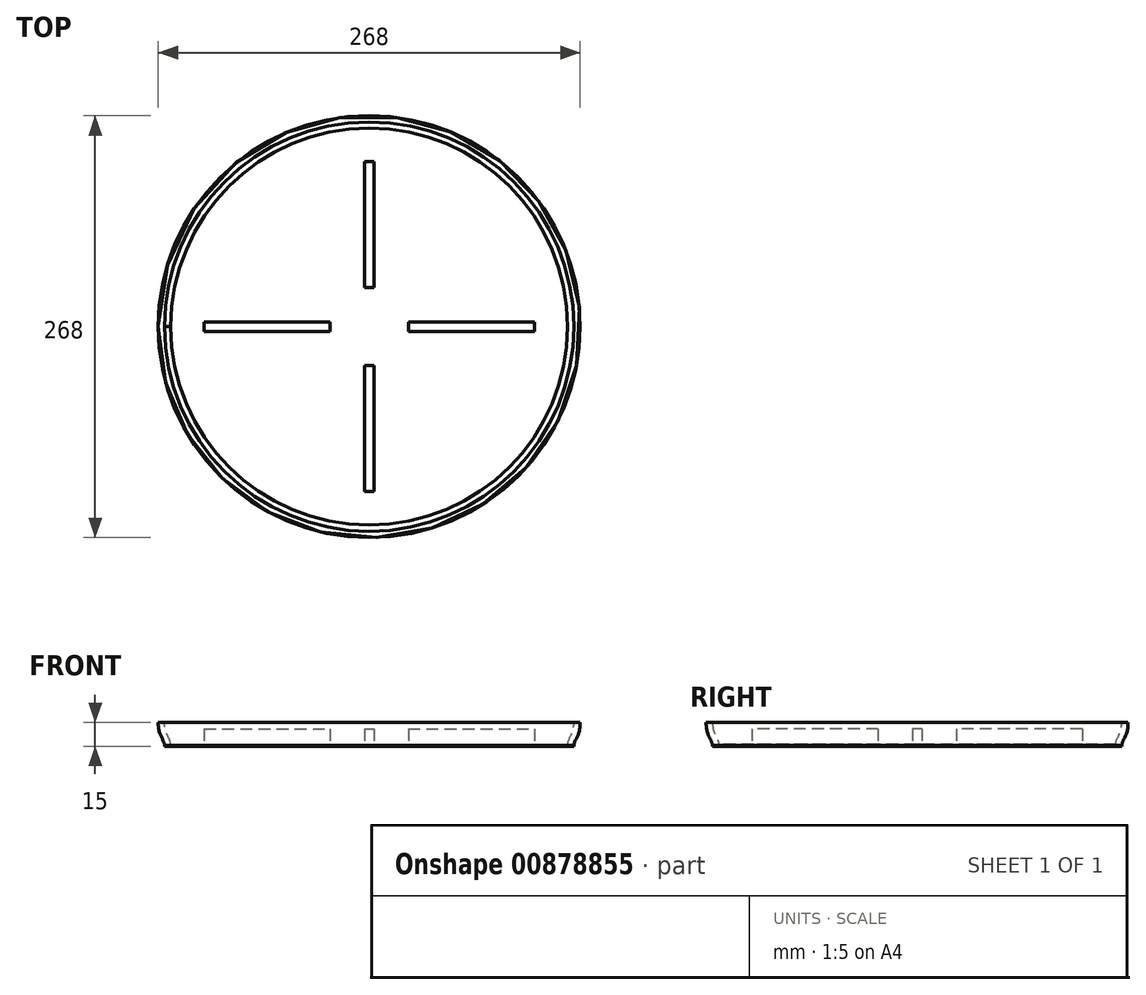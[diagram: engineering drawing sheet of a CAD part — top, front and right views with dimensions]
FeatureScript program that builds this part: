
annotation { "Feature Type Name" : "Feature", "Feature Type Description" : "" }
export const myFeature = defineFeature(function(context is Context, id is Id, definition is map)
    precondition{}
    {
        {
            var Q0;
            Q0=qCreatedBy(makeId("Top.planeOp"),FACE);
            var sketch = newSketch(context, id + "F0", { "sketchPlane" : qUnion([Q0])});
            skCircle(sketch, "E0", {"center": v(0, 0) * mm, "radius": 120 * mm, "construction": true});
            skCircle(sketch, "E1.0", {"center": v(0, 0) * mm, "radius": 126 * mm});
            skCircle(sketch, "E2.0", {"center": v(0, 0) * mm, "radius": 130 * mm});
            skSolve(sketch);
        }
        {
            var Q0;
            Q0=qCreatedBy(makeId("Front.planeOp"),FACE);
            var sketch = newSketch(context, id + "F1", { "sketchPlane" : qUnion([Q0])});
            skLineSegment(sketch, "E3", {"start": v(-126, 0) * mm, "end": v(-130, 0) * mm});
            skLineSegment(sketch, "E4", {"start": v(-126, 0) * mm, "end": v(-126, 13.8) * mm, "construction": true});
            skLineSegment(sketch, "E5", {"start": v(-130, 0) * mm, "end": v(-130, 15) * mm, "construction": true});
            skFitSpline(sketch, "E6", {"points": [v(-126, 0) * mm, v(-130, 15) * mm], "startDerivative": vector(0, 16.34) * mm, "endDerivative": vector(0, 22.5) * mm});
            skLineSegment(sketch, "E7", {"start": v(-130, 15) * mm, "end": v(-134, 15) * mm});
            skFitSpline(sketch, "E8.0", {"points": [v(-130, 0) * mm, v(-130, 0.44) * mm, v(-130.08, 1.18) * mm, v(-130.37, 2.24) * mm, v(-130.87, 3.47) * mm, v(-131.6, 4.97) * mm, v(-132.45, 6.83) * mm, v(-133.26, 9.1) * mm, v(-133.85, 11.8) * mm, v(-134, 13.88) * mm, v(-134, 15) * mm]});
            skLineSegment(sketch, "E9", {"start": v(0, 0) * mm, "end": v(0, 31.94) * mm, "construction": true});
            skSolve(sketch);
        }
        {
            var Q0;
            Q0=makeQuery(id+"F1.imprint","IMPRINT",FACE,{"disambiguationData":[TD([[makeQuery(id+"F1.imprint","IMPRINT",EDGE,{"derivedFrom":sQuery(id+"F1.wireOp",EDGE,"E3")}),-1.0]])]});
            var Q1;
            Q1=sQuery(id+"F1.wireOp",EDGE,"E9");
            revolve(context, id + "F2", {"surfaceOperationType" : NewSurfaceOperationType.NEW, "entities" : qUnion([Q0]), "axis" : qUnion([Q1]), "revolveType" : RevolveType.FULL});
        }
        {
            var Q0;
            Q0 = qSketchRegion(id + "F0", true);
            var Q1;
            Q1=makeQuery(id+"F0.imprint","IMPRINT",FACE,{"disambiguationData":[TD([[makeQuery(id+"F0.imprint","IMPRINT",EDGE,{"derivedFrom":sQuery(id+"F0.wireOp",EDGE,"E1.0")}),1.0]])]});
            extrude(context, id + "F3", {"entities" : qUnion([Q0, Q1]), "operationType" : NewBodyOperationType.ADD, "depth" : 1 * mm, "offsetDistance" : 25 * mm});
        }
        {
            var Q0;
            Q0=makeQuery(id+"F3.opExtrude","CAP_FACE",FACE,{"disambiguationData":[OSD([sQuery(id+"F0.wireOp",EDGE,"E2.0")])],"isStart":false});
            var sketch = newSketch(context, id + "F4", { "sketchPlane" : qUnion([Q0])});
            skLineSegment(sketch, "E10.bottom", {"start": v(-3, 104.82) * mm, "end": v(3, 104.82) * mm});
            skLineSegment(sketch, "E10.top", {"start": v(-3, 24.82) * mm, "end": v(3, 24.82) * mm});
            skLineSegment(sketch, "E10.left", {"start": v(-3, 104.82) * mm, "end": v(-3, 24.82) * mm});
            skLineSegment(sketch, "E10.right", {"start": v(3, 104.82) * mm, "end": v(3, 24.82) * mm});
            skLineSegment(sketch, "E11.bottom", {"start": v(-104.82, 3) * mm, "end": v(-24.82, 3) * mm});
            skLineSegment(sketch, "E11.top", {"start": v(-104.82, -3) * mm, "end": v(-24.82, -3) * mm});
            skLineSegment(sketch, "E11.left", {"start": v(-104.82, 3) * mm, "end": v(-104.82, -3) * mm});
            skLineSegment(sketch, "E11.right", {"start": v(-24.82, 3) * mm, "end": v(-24.82, -3) * mm});
            skLineSegment(sketch, "E12.bottom", {"start": v(24.82, 3) * mm, "end": v(104.82, 3) * mm});
            skLineSegment(sketch, "E12.top", {"start": v(24.82, -3) * mm, "end": v(104.82, -3) * mm});
            skLineSegment(sketch, "E12.left", {"start": v(24.82, 3) * mm, "end": v(24.82, -3) * mm});
            skLineSegment(sketch, "E12.right", {"start": v(104.82, 3) * mm, "end": v(104.82, -3) * mm});
            skLineSegment(sketch, "E13.bottom", {"start": v(-3, -24.82) * mm, "end": v(3, -24.82) * mm});
            skLineSegment(sketch, "E13.top", {"start": v(-3, -104.82) * mm, "end": v(3, -104.82) * mm});
            skLineSegment(sketch, "E13.left", {"start": v(-3, -24.82) * mm, "end": v(-3, -104.82) * mm});
            skLineSegment(sketch, "E13.right", {"start": v(3, -24.82) * mm, "end": v(3, -104.82) * mm});
            skCircle(sketch, "E14", {"center": v(0, 0) * mm, "radius": 25 * mm, "construction": true});
            skPoint(sketch, "E15", {"position": v(-104.82, 0) * mm});
            skPoint(sketch, "E16", {"position": v(0, -104.82) * mm});
            skPoint(sketch, "E17", {"position": v(104.82, 0) * mm});
            skPoint(sketch, "E18", {"position": v(0, 24.82) * mm});
            skSolve(sketch);
        }
        {
            var Q0;
            Q0 = qSketchRegion(id + "F4", true);
            extrude(context, id + "F5", {"entities" : qUnion([Q0]), "operationType" : NewBodyOperationType.ADD, "depth" : 10 * mm, "offsetDistance" : 25 * mm});
        }
    });
